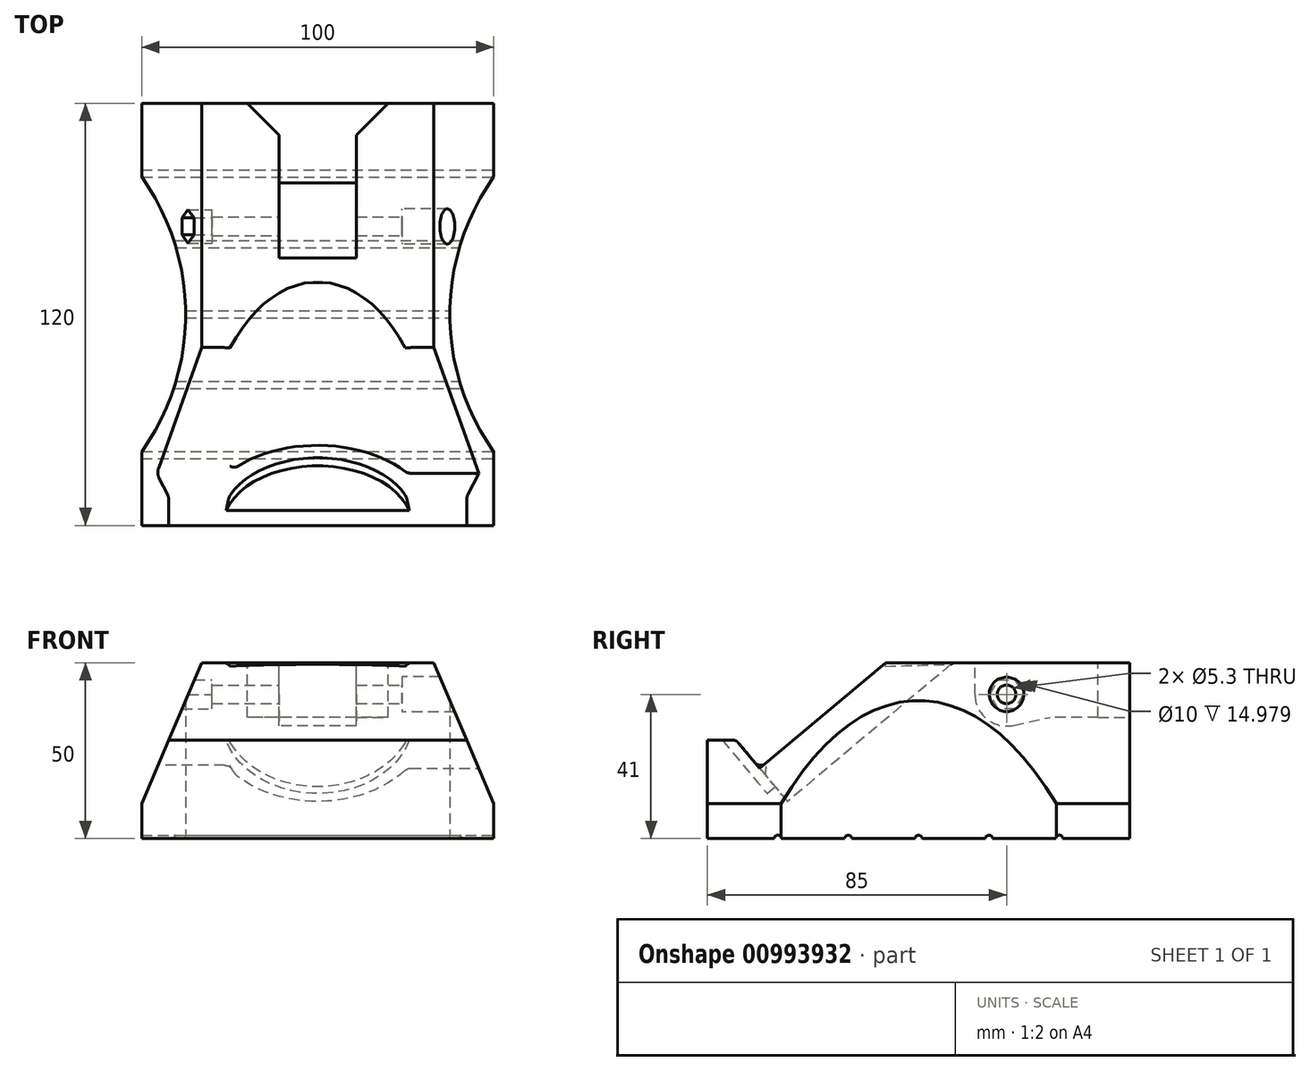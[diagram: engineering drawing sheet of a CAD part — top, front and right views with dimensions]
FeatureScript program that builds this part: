
annotation { "Feature Type Name" : "Feature", "Feature Type Description" : "" }
export const myFeature = defineFeature(function(context is Context, id is Id, definition is map)
    precondition{}
    {
        {
            var Q0;
            Q0=qCreatedBy(makeId("Front.planeOp"),FACE);
            var sketch = newSketch(context, id + "F0", { "sketchPlane" : qUnion([Q0])});
            skLineSegment(sketch, "E0", {"start": v(0, 0) * mm, "end": v(0, 50) * mm});
            skLineSegment(sketch, "E1", {"start": v(0, 50) * mm, "end": v(-33, 50) * mm});
            skLineSegment(sketch, "E2", {"start": v(-33, 50) * mm, "end": v(-50, 10) * mm});
            skLineSegment(sketch, "E3", {"start": v(-50, 10) * mm, "end": v(-50, 0) * mm});
            skLineSegment(sketch, "E4", {"start": v(-50, 0) * mm, "end": v(0, 0) * mm});
            skLineSegment(sketch, "E5.MirrorCS", {"start": v(0, 50) * mm, "end": v(33, 50) * mm});
            skLineSegment(sketch, "E6.MirrorCS", {"start": v(33, 50) * mm, "end": v(50, 10) * mm});
            skLineSegment(sketch, "E7.MirrorCS", {"start": v(50, 10) * mm, "end": v(50, 0) * mm});
            skLineSegment(sketch, "E8.MirrorCS", {"start": v(50, 0) * mm, "end": v(0, 0) * mm});
            skSolve(sketch);
        }
        {
            var Q0;
            Q0 = qSketchRegion(id + "F0", true);
            extrude(context, id + "F1", {"entities" : qUnion([Q0]), "depth" : 120 * mm, "offsetDistance" : 25 * mm});
        }
        {
            var Q0;
            Q0=qCreatedBy(makeId("Right.planeOp"),FACE);
            var sketch = newSketch(context, id + "F2", { "sketchPlane" : qUnion([Q0])});
            skLineSegment(sketch, "E9", {"start": v(0, 34.5) * mm, "end": v(-28.78, 34.5) * mm});
            skLineSegment(sketch, "E10", {"start": v(0, 41) * mm, "end": v(-48.15, 41) * mm, "construction": true});
            skCircle(sketch, "E11", {"center": v(-35, 41) * mm, "radius": 9 * mm});
            skLineSegment(sketch, "E12.MirrorCS", {"start": v(0, 47.5) * mm, "end": v(-28.78, 47.5) * mm});
            skLineSegment(sketch, "E13", {"start": v(0, 34.5) * mm, "end": v(0, 47.5) * mm});
            skCircle(sketch, "E14", {"center": v(-35, 41) * mm, "radius": 2.65 * mm});
            skLineSegment(sketch, "E15", {"start": v(0, 47.5) * mm, "end": v(0, 56.63) * mm});
            skLineSegment(sketch, "E16", {"start": v(-35.09, 50) * mm, "end": v(0, 56.63) * mm});
            skLineSegment(sketch, "E17", {"start": v(-33.08, 32.2) * mm, "end": v(-22.6, 34.5) * mm});
            skLineSegment(sketch, "E18", {"start": v(-44, 41) * mm, "end": v(-44, 53.05) * mm});
            skLineSegment(sketch, "E19", {"start": v(-44, 53.05) * mm, "end": v(-27.13, 51.5) * mm});
            skSolve(sketch);
        }
        {
            var Q0;
            Q0=makeQuery(id+"F2.imprint","IMPRINT",FACE,{"disambiguationData":[TD([[makeQuery(id+"F2.imprint","IMPRINT",EDGE,{"derivedFrom":sQuery(id+"F2.wireOp",EDGE,"E14")}),1.0]])]});
            extrude(context, id + "F3", {"entities" : qUnion([Q0]), "operationType" : NewBodyOperationType.REMOVE, "endBound" : BoundingType.SYMMETRIC, "oppositeDirection" : true, "depth" : 100 * mm, "offsetDistance" : 25 * mm});
        }
        {
            var Q0;
            Q0 = qSketchRegion(id + "F2", true);
            extrude(context, id + "F4", {"entities" : qUnion([Q0]), "operationType" : NewBodyOperationType.REMOVE, "endBound" : BoundingType.SYMMETRIC, "depth" : 22 * mm, "offsetDistance" : 25 * mm});
        }
        {
            var Q0;
            Q0=qCreatedBy(makeId("Right.planeOp"),FACE);
            cPlane(context, id + "F5", {"entities" : qUnion([Q0]), "cplaneType" : CPlaneType.OFFSET, "offset" : 24 * mm, "width" : 150 * mm, "height" : 150 * mm});
        }
        {
            var Q0;
            Q0=qCreatedBy(id+"F5.planeOp",FACE);
            var sketch = newSketch(context, id + "F6", { "sketchPlane" : qUnion([Q0])});
            skCircle(sketch, "E20.0", {"center": v(-35, 41) * mm, "radius": 2.65 * mm});
            skCircle(sketch, "E21", {"center": v(-35, 41) * mm, "radius": 5 * mm});
            skSolve(sketch);
        }
        {
            var Q0;
            Q0 = qSketchRegion(id + "F6", true);
            extrude(context, id + "F7", {"entities" : qUnion([Q0]), "operationType" : NewBodyOperationType.REMOVE, "depth" : 25 * mm, "offsetDistance" : 25 * mm});
        }
        {
            var Q0;
            Q0=qCreatedBy(makeId("Right.planeOp"),FACE);
            cPlane(context, id + "F8", {"entities" : qUnion([Q0]), "cplaneType" : CPlaneType.OFFSET, "offset" : 30 * mm, "oppositeDirection" : true, "width" : 150 * mm, "height" : 150 * mm});
        }
        {
            var Q0;
            Q0=qCreatedBy(id+"F8.planeOp",FACE);
            var sketch = newSketch(context, id + "F9", { "sketchPlane" : qUnion([Q0])});
            skCircle(sketch, "E22.0", {"center": v(-35, 41) * mm, "radius": 5 * mm, "construction": true});
            skCircle(sketch, "E23.cCircle", {"center": v(-35, 41) * mm, "radius": 4.15 * mm, "construction": true});
            skLineSegment(sketch, "E23.0", {"start": v(-37.4, 36.85) * mm, "end": v(-39.8, 41) * mm});
            skLineSegment(sketch, "E23.1", {"start": v(-39.8, 41) * mm, "end": v(-37.4, 45.15) * mm});
            skLineSegment(sketch, "E23.2", {"start": v(-37.4, 45.15) * mm, "end": v(-32.6, 45.15) * mm});
            skLineSegment(sketch, "E23.3", {"start": v(-32.6, 45.15) * mm, "end": v(-30.2, 41) * mm});
            skLineSegment(sketch, "E23.4", {"start": v(-30.2, 41) * mm, "end": v(-32.6, 36.85) * mm});
            skLineSegment(sketch, "E23.5", {"start": v(-32.6, 36.85) * mm, "end": v(-37.4, 36.85) * mm});
            skPoint(sketch, "E23.0.midPoint", {"position": v(-38.6, 38.93) * mm});
            skSolve(sketch);
        }
        {
            var Q0;
            Q0 = qSketchRegion(id + "F9", true);
            extrude(context, id + "F10", {"entities" : qUnion([Q0]), "operationType" : NewBodyOperationType.REMOVE, "oppositeDirection" : true, "depth" : 25 * mm, "offsetDistance" : 25 * mm});
        }
        {
            var Q0;
            Q0=makeQuery(id+"F1.opExtrude","SWEPT_FACE",FACE,{"disambiguationData":[OSD([sQuery(id+"F0.wireOp",EDGE,"E1"),sQuery(id+"F0.wireOp",EDGE,"E5.MirrorCS")])]});
            var sketch = newSketch(context, id + "F11", { "sketchPlane" : qUnion([Q0])});
            skLineSegment(sketch, "E24.0", {"start": v(-11, 0) * mm, "end": v(-11, -22.6) * mm, "construction": true});
            skLineSegment(sketch, "E25", {"start": v(0, -9) * mm, "end": v(-11, -9) * mm});
            skLineSegment(sketch, "E26", {"start": v(-11, -9) * mm, "end": v(-20, 0) * mm});
            skLineSegment(sketch, "E27", {"start": v(-20, 0) * mm, "end": v(0, 0) * mm});
            skLineSegment(sketch, "E28", {"start": v(0, 0) * mm, "end": v(0, -9) * mm});
            skLineSegment(sketch, "E29.MirrorCS", {"start": v(0, -9) * mm, "end": v(11, -9) * mm});
            skLineSegment(sketch, "E30.MirrorCS", {"start": v(20, 0) * mm, "end": v(0, 0) * mm});
            skLineSegment(sketch, "E31.MirrorCS", {"start": v(11, -9) * mm, "end": v(20, 0) * mm});
            skLineSegment(sketch, "E32.0", {"start": v(-11, 0) * mm, "end": v(-33, 0) * mm});
            skSolve(sketch);
        }
        {
            var Q0;
            {var subQ0=sQuery(id+"F11.wireOp",EDGE,"E28");var subQ1=makeQuery(id+"F11.imprint","IMPRINT",EDGE,{"derivedFrom":subQ0});var subQ21=sQuery(id+"F11.wireOp",EDGE,"E31.MirrorCS");var subQ23=sQuery(id+"F11.wireOp",EDGE,"E25");var subQ26=sQuery(id+"F11.wireOp",EDGE,"E26");Q0=qUnion([makeQuery(id+"F11.imprint","IMPRINT",FACE,{"disambiguationData":[TD([[makeQuery(id+"F11.imprint","IMPRINT",EDGE,{"derivedFrom":subQ26}),-1.0]])]}),makeQuery(id+"F11.imprint","IMPRINT",FACE,{"disambiguationData":[TD([[makeQuery(id+"F11.imprint","IMPRINT",EDGE,{"derivedFrom":subQ21}),1.0]])]}),makeQuery(id+"F11.imprint","IMPRINT",FACE,{"disambiguationData":[TD([[makeQuery(id+"F11.imprint","IMPRINT",EDGE,{"derivedFrom":subQ23}),-1.0]])]}),makeQuery(id+"F11.imprint","IMPRINT",FACE,{"disambiguationData":[TD([[subQ1,1.0]])]})]);}
            var Q1;
            Q1=makeQuery(id+"F4.boolean.opBoolean","COPY",FACE,{"derivedFrom":makeQuery(id+"F4.opExtrude","SWEPT_FACE",FACE,{"disambiguationData":[OSD([sQuery(id+"F2.wireOp",EDGE,"E9")])]})});
            extrude(context, id + "F12", {"entities" : qUnion([Q0]), "operationType" : NewBodyOperationType.REMOVE, "endBound" : BoundingType.UP_TO_SURFACE, "oppositeDirection" : true, "depth" : 25 * mm, "endBoundEntityFace" : qUnion([Q1]), "offsetDistance" : 25 * mm});
        }
        {
            var Q0;
            Q0=makeQuery(id+"F1.opExtrude","SWEPT_FACE",FACE,{"disambiguationData":[OSD([sQuery(id+"F0.wireOp",EDGE,"E7.MirrorCS")])]});
            var sketch = newSketch(context, id + "F13", { "sketchPlane" : qUnion([Q0])});
            skLineSegment(sketch, "E33", {"start": v(-33.73, 79.92) * mm, "end": v(-105.14, 20) * mm});
            skLineSegment(sketch, "E34", {"start": v(-105.14, 20) * mm, "end": v(-151.3, 75.02) * mm});
            skLineSegment(sketch, "E35", {"start": v(-33.73, 79.92) * mm, "end": v(-151.3, 75.02) * mm});
            skLineSegment(sketch, "E36.0", {"start": v(-120, 50) * mm, "end": v(-120, 10) * mm});
            skLineSegment(sketch, "E37", {"start": v(-111.86, 28) * mm, "end": v(-120, 28) * mm});
            skSolve(sketch);
        }
        {
            var Q0;
            Q0 = qSketchRegion(id + "F13", true);
            extrude(context, id + "F14", {"entities" : qUnion([Q0]), "operationType" : NewBodyOperationType.REMOVE, "endBound" : BoundingType.THROUGH_ALL, "oppositeDirection" : true, "depth" : 25 * mm, "offsetDistance" : 25 * mm});
        }
        {
            var Q0;
            Q0=makeQuery(id+"F14.boolean.opBoolean","COPY",FACE,{"derivedFrom":makeQuery(id+"F14.opExtrude","SWEPT_FACE",FACE,{"disambiguationData":[OSD([sQuery(id+"F13.wireOp",EDGE,"E34")])]})});
            var sketch = newSketch(context, id + "F15", { "sketchPlane" : qUnion([Q0])});
            skLineSegment(sketch, "E38.0", {"start": v(-11, 66.58) * mm, "end": v(11, 66.58) * mm});
            skLineSegment(sketch, "E39.0", {"start": v(45.75, 82.9) * mm, "end": v(-45.75, 82.9) * mm, "construction": true});
            skPoint(sketch, "E40", {"position": v(0, 106.02) * mm});
            skCircle(sketch, "E41", {"center": v(0, 103.08) * mm, "radius": 32.5 * mm});
            skSolve(sketch);
        }
        {
            var Q0;
            Q0 = qSketchRegion(id + "F15", true);
            var Q1;
            Q1 = qConstructionFilter(qBodyType(qCreatedBy(id + "F15" ,EDGE), BodyType.WIRE), ConstructionObject.NO);
            extrude(context, id + "F16", {"entities" : qUnion([Q0]), "operationType" : NewBodyOperationType.REMOVE, "surfaceEntities" : qUnion([Q1]), "depth" : 100 * mm, "offsetDistance" : 25 * mm});
        }
        {
            var Q0;
            {var subQ0=sQuery(id+"F15.wireOp",EDGE,"E41");var subQ1=sQuery(id+"F13.wireOp",EDGE,"E34");var subQ4=makeQuery(id+"F14.boolean.opBoolean","COPY",EDGE,{"derivedFrom":makeQuery(id+"F14.opExtrude","SWEPT_EDGE",EDGE,{"disambiguationData":[OSD([sQuery(id+"F13.wireOp",EDGE,"E33"),subQ1])]})});var subQ5=makeQuery(id+"F15.imprint","INTERSECT",VERTEX,{"disambiguationData":[OD(0.0)],"derivedFrom":[subQ4,subQ0]});Q0=makeQuery(id+"F15.imprint","IMPRINT",FACE,{"disambiguationData":[TD([[makeQuery(id+"F15.imprint","IMPRINT",EDGE,{"disambiguationData":[TD([[subQ5,1.0]])],"derivedFrom":subQ4}),-1.0]])]});}
            var sketch = newSketch(context, id + "F17", { "sketchPlane" : qUnion([Q0])});
            skPoint(sketch, "E42.0", {"position": v(0, 103.08) * mm});
            skCircle(sketch, "E43", {"center": v(0, 103.08) * mm, "radius": 27 * mm});
            skSolve(sketch);
        }
        {
            var Q0;
            Q0 = qSketchRegion(id + "F17", true);
            extrude(context, id + "F18", {"entities" : qUnion([Q0]), "operationType" : NewBodyOperationType.REMOVE, "oppositeDirection" : true, "depth" : 3 * mm, "offsetDistance" : 25 * mm});
        }
        {
            var Q0;
            Q0=makeQuery(id+"F1.opExtrude","SWEPT_FACE",FACE,{"disambiguationData":[OSD([sQuery(id+"F0.wireOp",EDGE,"E7.MirrorCS")])]});
            var sketch = newSketch(context, id + "F19", { "sketchPlane" : qUnion([Q0])});
            skCircle(sketch, "E44", {"center": v(-20, 0) * mm, "radius": 1 * mm});
            skCircle(sketch, "E45.1.0.0", {"center": v(-40, 0) * mm, "radius": 1 * mm});
            skCircle(sketch, "E45.2.0.0", {"center": v(-60, 0) * mm, "radius": 1 * mm});
            skCircle(sketch, "E45.3.0.0", {"center": v(-80, 0) * mm, "radius": 1 * mm});
            skCircle(sketch, "E45.4.0.0", {"center": v(-100, 0) * mm, "radius": 1 * mm});
            skLineSegment(sketch, "E45.direction1", {"start": v(-20, 0) * mm, "end": v(-40, 0) * mm, "construction": true});
            skSolve(sketch);
        }
        {
            var Q0;
            Q0 = qSketchRegion(id + "F19", true);
            extrude(context, id + "F20", {"entities" : qUnion([Q0]), "operationType" : NewBodyOperationType.REMOVE, "endBound" : BoundingType.THROUGH_ALL, "oppositeDirection" : true, "depth" : 25 * mm, "offsetDistance" : 25 * mm});
        }
        {
            var Q0;
            Q0=qCreatedBy(makeId("Top.planeOp"),FACE);
            var sketch = newSketch(context, id + "F21", { "sketchPlane" : qUnion([Q0])});
            skCircle(sketch, "E46", {"center": v(105, -60) * mm, "radius": 67.5 * mm});
            skCircle(sketch, "E47.MirrorC", {"center": v(-105, -60) * mm, "radius": 67.5 * mm});
            skSolve(sketch);
        }
        {
            var Q0;
            Q0 = qSketchRegion(id + "F21", true);
            extrude(context, id + "F22", {"entities" : qUnion([Q0]), "operationType" : NewBodyOperationType.REMOVE, "endBound" : BoundingType.THROUGH_ALL, "depth" : 25 * mm, "offsetDistance" : 25 * mm});
        }
        {
            var Q0;
            Q0=makeQuery(id+"F12.boolean.opBoolean","COPY",EDGE,{"derivedFrom":makeQuery(id+"F12.opExtrude","SWEPT_EDGE",EDGE,{"disambiguationData":[OSD([sQuery(id+"F0.wireOp",EDGE,"E1"),sQuery(id+"F0.wireOp",EDGE,"E5.MirrorCS"),sQuery(id+"F11.wireOp",EDGE,"E30.MirrorCS"),sQuery(id+"F11.wireOp",EDGE,"E31.MirrorCS")])]})});
            var Q1;
            Q1=makeQuery(id+"F12.boolean.opBoolean","COPY",EDGE,{"derivedFrom":makeQuery(id+"F12.opExtrude","SWEPT_EDGE",EDGE,{"disambiguationData":[OSD([sQuery(id+"F0.wireOp",EDGE,"E1"),sQuery(id+"F0.wireOp",EDGE,"E5.MirrorCS"),sQuery(id+"F2.wireOp",EDGE,"E9"),sQuery(id+"F2.wireOp",EDGE,"E11"),sQuery(id+"F2.wireOp",EDGE,"E13"),sQuery(id+"F2.wireOp",EDGE,"E14"),sQuery(id+"F2.wireOp",EDGE,"E15"),sQuery(id+"F2.wireOp",EDGE,"E16"),sQuery(id+"F2.wireOp",EDGE,"E17"),sQuery(id+"F2.wireOp",EDGE,"E18"),sQuery(id+"F2.wireOp",EDGE,"E19"),sQuery(id+"F11.wireOp",EDGE,"E29.MirrorCS"),sQuery(id+"F11.wireOp",EDGE,"E31.MirrorCS")])]})});
            var Q2;
            Q2=makeQuery(id+"F12.boolean.opBoolean","COPY",EDGE,{"derivedFrom":makeQuery(id+"F12.opExtrude","SWEPT_EDGE",EDGE,{"disambiguationData":[OSD([sQuery(id+"F0.wireOp",EDGE,"E1"),sQuery(id+"F0.wireOp",EDGE,"E5.MirrorCS"),sQuery(id+"F2.wireOp",EDGE,"E9"),sQuery(id+"F2.wireOp",EDGE,"E11"),sQuery(id+"F2.wireOp",EDGE,"E13"),sQuery(id+"F2.wireOp",EDGE,"E14"),sQuery(id+"F2.wireOp",EDGE,"E15"),sQuery(id+"F2.wireOp",EDGE,"E16"),sQuery(id+"F2.wireOp",EDGE,"E17"),sQuery(id+"F2.wireOp",EDGE,"E18"),sQuery(id+"F2.wireOp",EDGE,"E19"),sQuery(id+"F11.wireOp",EDGE,"E25"),sQuery(id+"F11.wireOp",EDGE,"E26")])]})});
            var Q3;
            Q3=makeQuery(id+"F12.boolean.opBoolean","COPY",EDGE,{"derivedFrom":makeQuery(id+"F12.opExtrude","SWEPT_EDGE",EDGE,{"disambiguationData":[OSD([sQuery(id+"F0.wireOp",EDGE,"E1"),sQuery(id+"F0.wireOp",EDGE,"E5.MirrorCS"),sQuery(id+"F11.wireOp",EDGE,"E30.MirrorCS"),sQuery(id+"F11.wireOp",EDGE,"E31.MirrorCS")])]})});
            var Q4;
            Q4=makeQuery(id+"F12.boolean.opBoolean","INTERSECT",EDGE,{"derivedFrom":[makeQuery(id+"FForsSt9jY7SkNF_1.boolean.opBoolean","COPY",FACE,{"derivedFrom":makeQuery(id+"FForsSt9jY7SkNF_1.opExtrude","SWEPT_FACE",FACE,{"disambiguationData":[OSD([sQuery(id+"FEJrApT3yMmYln8_1.wireOp",EDGE,"aShYpLVm-hpr0-Twte-arf6-uDWaxXaaRNYl")])]})}),makeQuery(id+"F12.opExtrude","SWEPT_FACE",FACE,{"disambiguationData":[OSD([sQuery(id+"F11.wireOp",EDGE,"E31.MirrorCS")])]})]});
            var Q5;
            Q5=makeQuery(id+"F12.boolean.opBoolean","INTERSECT",EDGE,{"derivedFrom":[makeQuery(id+"FForsSt9jY7SkNF_1.boolean.opBoolean","COPY",FACE,{"derivedFrom":makeQuery(id+"FForsSt9jY7SkNF_1.opExtrude","SWEPT_FACE",FACE,{"disambiguationData":[OSD([sQuery(id+"FEJrApT3yMmYln8_1.wireOp",EDGE,"aShYpLVm-hpr0-Twte-arf6-uDWaxXaaRNYl")])]})}),makeQuery(id+"F12.opExtrude","SWEPT_FACE",FACE,{"disambiguationData":[OSD([sQuery(id+"F11.wireOp",EDGE,"E26")])]})]});
            var Q6;
            Q6=makeQuery(id+"F16.boolean.opBoolean","INTERSECT",EDGE,{"disambiguationData":[OD(0.0)],"derivedFrom":[makeQuery(id+"F14.boolean.opBoolean","COPY",FACE,{"derivedFrom":makeQuery(id+"F14.opExtrude","SWEPT_FACE",FACE,{"disambiguationData":[OSD([sQuery(id+"F13.wireOp",EDGE,"E33")])]})}),makeQuery(id+"F16.opExtrude","SWEPT_FACE",FACE,{"disambiguationData":[OSD([sQuery(id+"F15.wireOp",EDGE,"E41")])]})]});
            var Q7;
            Q7=makeQuery(id+"F16.boolean.opBoolean","INTERSECT",EDGE,{"disambiguationData":[OD(1.0)],"derivedFrom":[makeQuery(id+"F14.boolean.opBoolean","COPY",FACE,{"derivedFrom":makeQuery(id+"F14.opExtrude","SWEPT_FACE",FACE,{"disambiguationData":[OSD([sQuery(id+"F13.wireOp",EDGE,"E33")])]})}),makeQuery(id+"F16.opExtrude","SWEPT_FACE",FACE,{"disambiguationData":[OSD([sQuery(id+"F15.wireOp",EDGE,"E41")])]})]});
            var Q8;
            Q8=makeQuery(id+"F16.boolean.opBoolean","INTERSECT",EDGE,{"derivedFrom":[makeQuery(id+"F1.opExtrude","SWEPT_FACE",FACE,{"disambiguationData":[OSD([sQuery(id+"F0.wireOp",EDGE,"E1"),sQuery(id+"F0.wireOp",EDGE,"E5.MirrorCS")])]}),makeQuery(id+"F16.opExtrude","SWEPT_FACE",FACE,{"disambiguationData":[OSD([sQuery(id+"F15.wireOp",EDGE,"E41")])]})]});
            var Q9;
            {var subQ0=sQuery(id+"F13.wireOp",EDGE,"E34");var subQ1=sQuery(id+"F13.wireOp",EDGE,"E37");Q9=makeQuery(id+"F18.boolean.opBoolean","SPLIT",EDGE,{"disambiguationData":[TD([makeQuery(id+"F1.opExtrude","SWEPT_FACE",FACE,{"disambiguationData":[OSD([sQuery(id+"F0.wireOp",EDGE,"E2")])]})])],"derivedFrom":makeQuery(id+"F14.boolean.opBoolean","COPY",EDGE,{"derivedFrom":makeQuery(id+"F14.opExtrude","SWEPT_EDGE",EDGE,{"disambiguationData":[OSD([subQ0,subQ1])]})})});}
            var Q10;
            {var subQ0=sQuery(id+"F13.wireOp",EDGE,"E37");var subQ1=sQuery(id+"F13.wireOp",EDGE,"E34");Q10=makeQuery(id+"F18.boolean.opBoolean","SPLIT",EDGE,{"disambiguationData":[TD([makeQuery(id+"F1.opExtrude","SWEPT_FACE",FACE,{"disambiguationData":[OSD([sQuery(id+"F0.wireOp",EDGE,"E6.MirrorCS")])]})])],"derivedFrom":makeQuery(id+"F14.boolean.opBoolean","COPY",EDGE,{"derivedFrom":makeQuery(id+"F14.opExtrude","SWEPT_EDGE",EDGE,{"disambiguationData":[OSD([subQ1,subQ0])]})})});}
            var Q11;
            {var subQ1=sQuery(id+"F13.wireOp",EDGE,"E34");var subQ2=sQuery(id+"F13.wireOp",EDGE,"E33");Q11=makeQuery(id+"F16.boolean.opBoolean","SPLIT",EDGE,{"disambiguationData":[TD([makeQuery(id+"F1.opExtrude","SWEPT_FACE",FACE,{"disambiguationData":[OSD([sQuery(id+"F0.wireOp",EDGE,"E2")])]})])],"derivedFrom":makeQuery(id+"F14.boolean.opBoolean","COPY",EDGE,{"derivedFrom":makeQuery(id+"F14.opExtrude","SWEPT_EDGE",EDGE,{"disambiguationData":[OSD([subQ2,subQ1])]})})});}
            fillet(context, id + "F23", {"entities" : qUnion([Q0, Q1, Q2, Q3, Q4, Q5, Q6, Q7, Q8, Q9, Q10, Q11]), "radius" : 2 * mm, "tangentPropagation" : true, "allowEdgeOverflow" : false});
        }
    });
